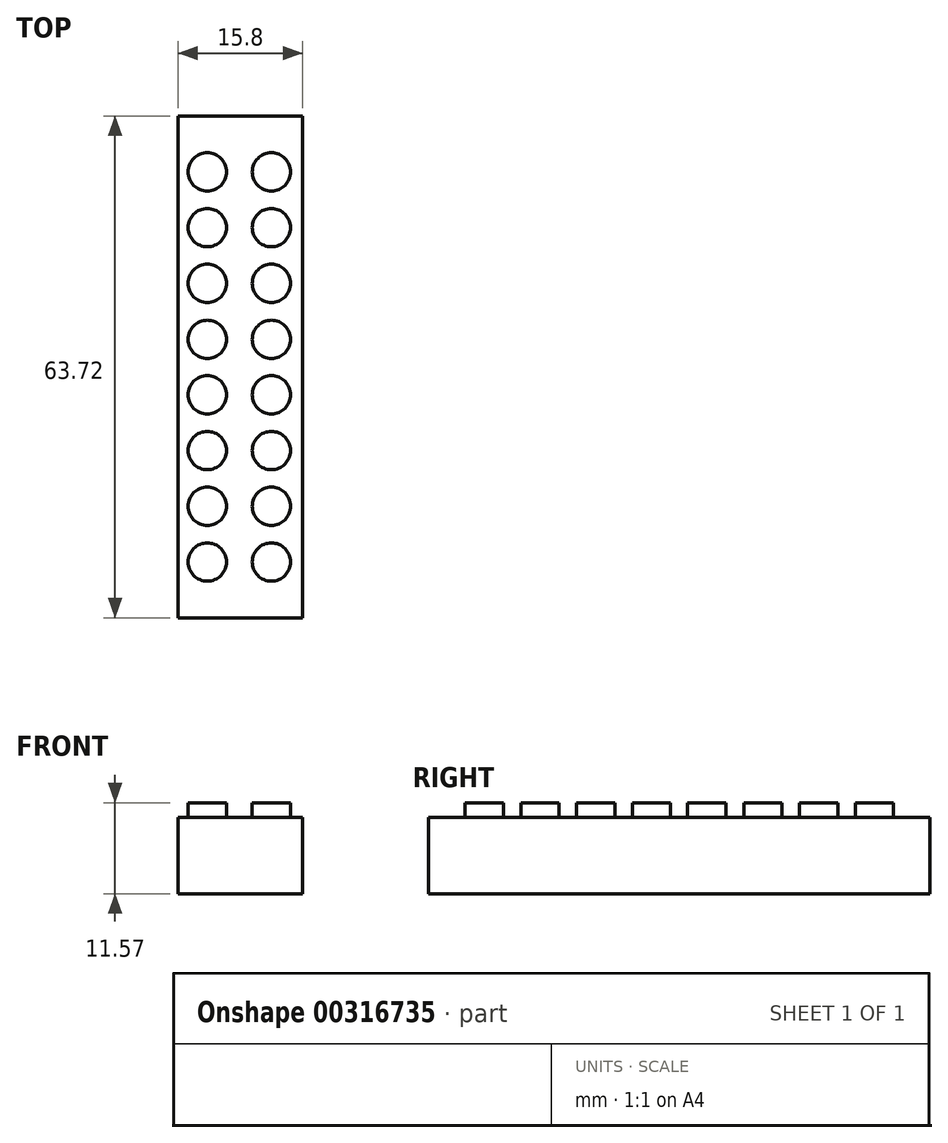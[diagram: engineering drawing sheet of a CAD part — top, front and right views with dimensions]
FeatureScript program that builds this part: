
annotation { "Feature Type Name" : "Feature", "Feature Type Description" : "" }
export const myFeature = defineFeature(function(context is Context, id is Id, definition is map)
    precondition{}
    {
        {
            var Q0;
            Q0=qCreatedBy(makeId("Top.planeOp"),FACE);
            var sketch = newSketch(context, id + "F0", { "sketchPlane" : qUnion([Q0])});
            skLineSegment(sketch, "E0", {"start": v(-59.65, 28.36) * mm, "end": v(-59.65, -35.36) * mm});
            skLineSegment(sketch, "E1", {"start": v(-59.65, -35.36) * mm, "end": v(-43.85, -35.36) * mm});
            skLineSegment(sketch, "E2", {"start": v(-43.85, -35.36) * mm, "end": v(-43.85, 28.36) * mm});
            skLineSegment(sketch, "E3", {"start": v(-43.85, 28.36) * mm, "end": v(-59.65, 28.36) * mm});
            skCircle(sketch, "E4", {"center": v(-55.94, 21.28) * mm, "radius": 2.43 * mm});
            skCircle(sketch, "E5", {"center": v(-55.94, 14.2) * mm, "radius": 2.43 * mm});
            skCircle(sketch, "E6", {"center": v(-55.94, 7.12) * mm, "radius": 2.43 * mm});
            skCircle(sketch, "E7", {"center": v(-55.94, 0) * mm, "radius": 2.43 * mm});
            skCircle(sketch, "E8", {"center": v(-55.94, -7.04) * mm, "radius": 2.43 * mm});
            skCircle(sketch, "E9", {"center": v(-55.94, -14.12) * mm, "radius": 2.43 * mm});
            skCircle(sketch, "E10", {"center": v(-55.94, -21.2) * mm, "radius": 2.43 * mm});
            skCircle(sketch, "E11", {"center": v(-55.94, -28.28) * mm, "radius": 2.43 * mm});
            skCircle(sketch, "E12", {"center": v(-47.8, 21.28) * mm, "radius": 2.43 * mm});
            skCircle(sketch, "E13", {"center": v(-47.8, 14.2) * mm, "radius": 2.43 * mm});
            skCircle(sketch, "E14", {"center": v(-47.8, 7.12) * mm, "radius": 2.43 * mm});
            skCircle(sketch, "E15", {"center": v(-47.8, 0) * mm, "radius": 2.43 * mm});
            skCircle(sketch, "E16", {"center": v(-47.8, -7.04) * mm, "radius": 2.43 * mm});
            skCircle(sketch, "E17", {"center": v(-47.8, -14.12) * mm, "radius": 2.43 * mm});
            skCircle(sketch, "E18", {"center": v(-47.8, -21.2) * mm, "radius": 2.43 * mm});
            skCircle(sketch, "E19", {"center": v(-47.8, -28.28) * mm, "radius": 2.43 * mm});
            skSolve(sketch);
        }
        {
            var Q0;
            Q0=makeQuery(id+"F0.imprint","IMPRINT",FACE,{"disambiguationData":[TD([[makeQuery(id+"F0.imprint","IMPRINT",EDGE,{"derivedFrom":sQuery(id+"F0.wireOp",EDGE,"E4")}),1.0]])]});
            var Q1;
            Q1=makeQuery(id+"F0.imprint","IMPRINT",FACE,{"disambiguationData":[TD([[makeQuery(id+"F0.imprint","IMPRINT",EDGE,{"derivedFrom":sQuery(id+"F0.wireOp",EDGE,"E5")}),1.0]])]});
            var Q2;
            Q2=makeQuery(id+"F0.imprint","IMPRINT",FACE,{"disambiguationData":[TD([[makeQuery(id+"F0.imprint","IMPRINT",EDGE,{"derivedFrom":sQuery(id+"F0.wireOp",EDGE,"E6")}),1.0]])]});
            var Q3;
            Q3=makeQuery(id+"F0.imprint","IMPRINT",FACE,{"disambiguationData":[TD([[makeQuery(id+"F0.imprint","IMPRINT",EDGE,{"derivedFrom":sQuery(id+"F0.wireOp",EDGE,"E7")}),1.0]])]});
            var Q4;
            Q4=makeQuery(id+"F0.imprint","IMPRINT",FACE,{"disambiguationData":[TD([[makeQuery(id+"F0.imprint","IMPRINT",EDGE,{"derivedFrom":sQuery(id+"F0.wireOp",EDGE,"E8")}),1.0]])]});
            var Q5;
            Q5=makeQuery(id+"F0.imprint","IMPRINT",FACE,{"disambiguationData":[TD([[makeQuery(id+"F0.imprint","IMPRINT",EDGE,{"derivedFrom":sQuery(id+"F0.wireOp",EDGE,"E9")}),1.0]])]});
            var Q6;
            Q6=makeQuery(id+"F0.imprint","IMPRINT",FACE,{"disambiguationData":[TD([[makeQuery(id+"F0.imprint","IMPRINT",EDGE,{"derivedFrom":sQuery(id+"F0.wireOp",EDGE,"E10")}),1.0]])]});
            var Q7;
            Q7=makeQuery(id+"F0.imprint","IMPRINT",FACE,{"disambiguationData":[TD([[makeQuery(id+"F0.imprint","IMPRINT",EDGE,{"derivedFrom":sQuery(id+"F0.wireOp",EDGE,"E11")}),1.0]])]});
            var Q8;
            Q8=makeQuery(id+"F0.imprint","IMPRINT",FACE,{"disambiguationData":[TD([[makeQuery(id+"F0.imprint","IMPRINT",EDGE,{"derivedFrom":sQuery(id+"F0.wireOp",EDGE,"E19")}),1.0]])]});
            var Q9;
            Q9=makeQuery(id+"F0.imprint","IMPRINT",FACE,{"disambiguationData":[TD([[makeQuery(id+"F0.imprint","IMPRINT",EDGE,{"derivedFrom":sQuery(id+"F0.wireOp",EDGE,"E18")}),1.0]])]});
            var Q10;
            Q10=makeQuery(id+"F0.imprint","IMPRINT",FACE,{"disambiguationData":[TD([[makeQuery(id+"F0.imprint","IMPRINT",EDGE,{"derivedFrom":sQuery(id+"F0.wireOp",EDGE,"E17")}),1.0]])]});
            var Q11;
            Q11=makeQuery(id+"F0.imprint","IMPRINT",FACE,{"disambiguationData":[TD([[makeQuery(id+"F0.imprint","IMPRINT",EDGE,{"derivedFrom":sQuery(id+"F0.wireOp",EDGE,"E16")}),1.0]])]});
            var Q12;
            Q12=makeQuery(id+"F0.imprint","IMPRINT",FACE,{"disambiguationData":[TD([[makeQuery(id+"F0.imprint","IMPRINT",EDGE,{"derivedFrom":sQuery(id+"F0.wireOp",EDGE,"E15")}),1.0]])]});
            var Q13;
            Q13=makeQuery(id+"F0.imprint","IMPRINT",FACE,{"disambiguationData":[TD([[makeQuery(id+"F0.imprint","IMPRINT",EDGE,{"derivedFrom":sQuery(id+"F0.wireOp",EDGE,"E14")}),1.0]])]});
            var Q14;
            Q14=makeQuery(id+"F0.imprint","IMPRINT",FACE,{"disambiguationData":[TD([[makeQuery(id+"F0.imprint","IMPRINT",EDGE,{"derivedFrom":sQuery(id+"F0.wireOp",EDGE,"E13")}),1.0]])]});
            var Q15;
            Q15=makeQuery(id+"F0.imprint","IMPRINT",FACE,{"disambiguationData":[TD([[makeQuery(id+"F0.imprint","IMPRINT",EDGE,{"derivedFrom":sQuery(id+"F0.wireOp",EDGE,"E12")}),1.0]])]});
            var Q16;
            Q16=makeQuery(id+"F0.imprint","IMPRINT",FACE,{"disambiguationData":[TD([[makeQuery(id+"F0.imprint","IMPRINT",EDGE,{"derivedFrom":sQuery(id+"F0.wireOp",EDGE,"E0")}),1.0]])]});
            extrude(context, id + "F1", {"entities" : qUnion([Q0, Q1, Q2, Q3, Q4, Q5, Q6, Q7, Q8, Q9, Q10, Q11, Q12, Q13, Q14, Q15, Q16]), "oppositeDirection" : true, "depth" : 9.71 * mm});
        }
        {
            var Q0;
            Q0=makeQuery(id+"F0.imprint","IMPRINT",FACE,{"disambiguationData":[TD([[makeQuery(id+"F0.imprint","IMPRINT",EDGE,{"derivedFrom":sQuery(id+"F0.wireOp",EDGE,"E4")}),1.0]])]});
            var Q1;
            Q1=makeQuery(id+"F0.imprint","IMPRINT",FACE,{"disambiguationData":[TD([[makeQuery(id+"F0.imprint","IMPRINT",EDGE,{"derivedFrom":sQuery(id+"F0.wireOp",EDGE,"E5")}),1.0]])]});
            var Q2;
            Q2=makeQuery(id+"F0.imprint","IMPRINT",FACE,{"disambiguationData":[TD([[makeQuery(id+"F0.imprint","IMPRINT",EDGE,{"derivedFrom":sQuery(id+"F0.wireOp",EDGE,"E6")}),1.0]])]});
            var Q3;
            Q3=makeQuery(id+"F0.imprint","IMPRINT",FACE,{"disambiguationData":[TD([[makeQuery(id+"F0.imprint","IMPRINT",EDGE,{"derivedFrom":sQuery(id+"F0.wireOp",EDGE,"E7")}),1.0]])]});
            var Q4;
            Q4=makeQuery(id+"F0.imprint","IMPRINT",FACE,{"disambiguationData":[TD([[makeQuery(id+"F0.imprint","IMPRINT",EDGE,{"derivedFrom":sQuery(id+"F0.wireOp",EDGE,"E8")}),1.0]])]});
            var Q5;
            Q5=makeQuery(id+"F0.imprint","IMPRINT",FACE,{"disambiguationData":[TD([[makeQuery(id+"F0.imprint","IMPRINT",EDGE,{"derivedFrom":sQuery(id+"F0.wireOp",EDGE,"E9")}),1.0]])]});
            var Q6;
            Q6=makeQuery(id+"F0.imprint","IMPRINT",FACE,{"disambiguationData":[TD([[makeQuery(id+"F0.imprint","IMPRINT",EDGE,{"derivedFrom":sQuery(id+"F0.wireOp",EDGE,"E10")}),1.0]])]});
            var Q7;
            Q7=makeQuery(id+"F0.imprint","IMPRINT",FACE,{"disambiguationData":[TD([[makeQuery(id+"F0.imprint","IMPRINT",EDGE,{"derivedFrom":sQuery(id+"F0.wireOp",EDGE,"E11")}),1.0]])]});
            var Q8;
            Q8=makeQuery(id+"F0.imprint","IMPRINT",FACE,{"disambiguationData":[TD([[makeQuery(id+"F0.imprint","IMPRINT",EDGE,{"derivedFrom":sQuery(id+"F0.wireOp",EDGE,"E19")}),1.0]])]});
            var Q9;
            Q9=makeQuery(id+"F0.imprint","IMPRINT",FACE,{"disambiguationData":[TD([[makeQuery(id+"F0.imprint","IMPRINT",EDGE,{"derivedFrom":sQuery(id+"F0.wireOp",EDGE,"E18")}),1.0]])]});
            var Q10;
            Q10=makeQuery(id+"F0.imprint","IMPRINT",FACE,{"disambiguationData":[TD([[makeQuery(id+"F0.imprint","IMPRINT",EDGE,{"derivedFrom":sQuery(id+"F0.wireOp",EDGE,"E17")}),1.0]])]});
            var Q11;
            Q11=makeQuery(id+"F0.imprint","IMPRINT",FACE,{"disambiguationData":[TD([[makeQuery(id+"F0.imprint","IMPRINT",EDGE,{"derivedFrom":sQuery(id+"F0.wireOp",EDGE,"E16")}),1.0]])]});
            var Q12;
            Q12=makeQuery(id+"F0.imprint","IMPRINT",FACE,{"disambiguationData":[TD([[makeQuery(id+"F0.imprint","IMPRINT",EDGE,{"derivedFrom":sQuery(id+"F0.wireOp",EDGE,"E15")}),1.0]])]});
            var Q13;
            Q13=makeQuery(id+"F0.imprint","IMPRINT",FACE,{"disambiguationData":[TD([[makeQuery(id+"F0.imprint","IMPRINT",EDGE,{"derivedFrom":sQuery(id+"F0.wireOp",EDGE,"E14")}),1.0]])]});
            var Q14;
            Q14=makeQuery(id+"F0.imprint","IMPRINT",FACE,{"disambiguationData":[TD([[makeQuery(id+"F0.imprint","IMPRINT",EDGE,{"derivedFrom":sQuery(id+"F0.wireOp",EDGE,"E13")}),1.0]])]});
            var Q15;
            Q15=makeQuery(id+"F0.imprint","IMPRINT",FACE,{"disambiguationData":[TD([[makeQuery(id+"F0.imprint","IMPRINT",EDGE,{"derivedFrom":sQuery(id+"F0.wireOp",EDGE,"E12")}),1.0]])]});
            extrude(context, id + "F2", {"entities" : qUnion([Q0, Q1, Q2, Q3, Q4, Q5, Q6, Q7, Q8, Q9, Q10, Q11, Q12, Q13, Q14, Q15]), "operationType" : NewBodyOperationType.ADD, "depth" : 1.86 * mm});
        }
    });
